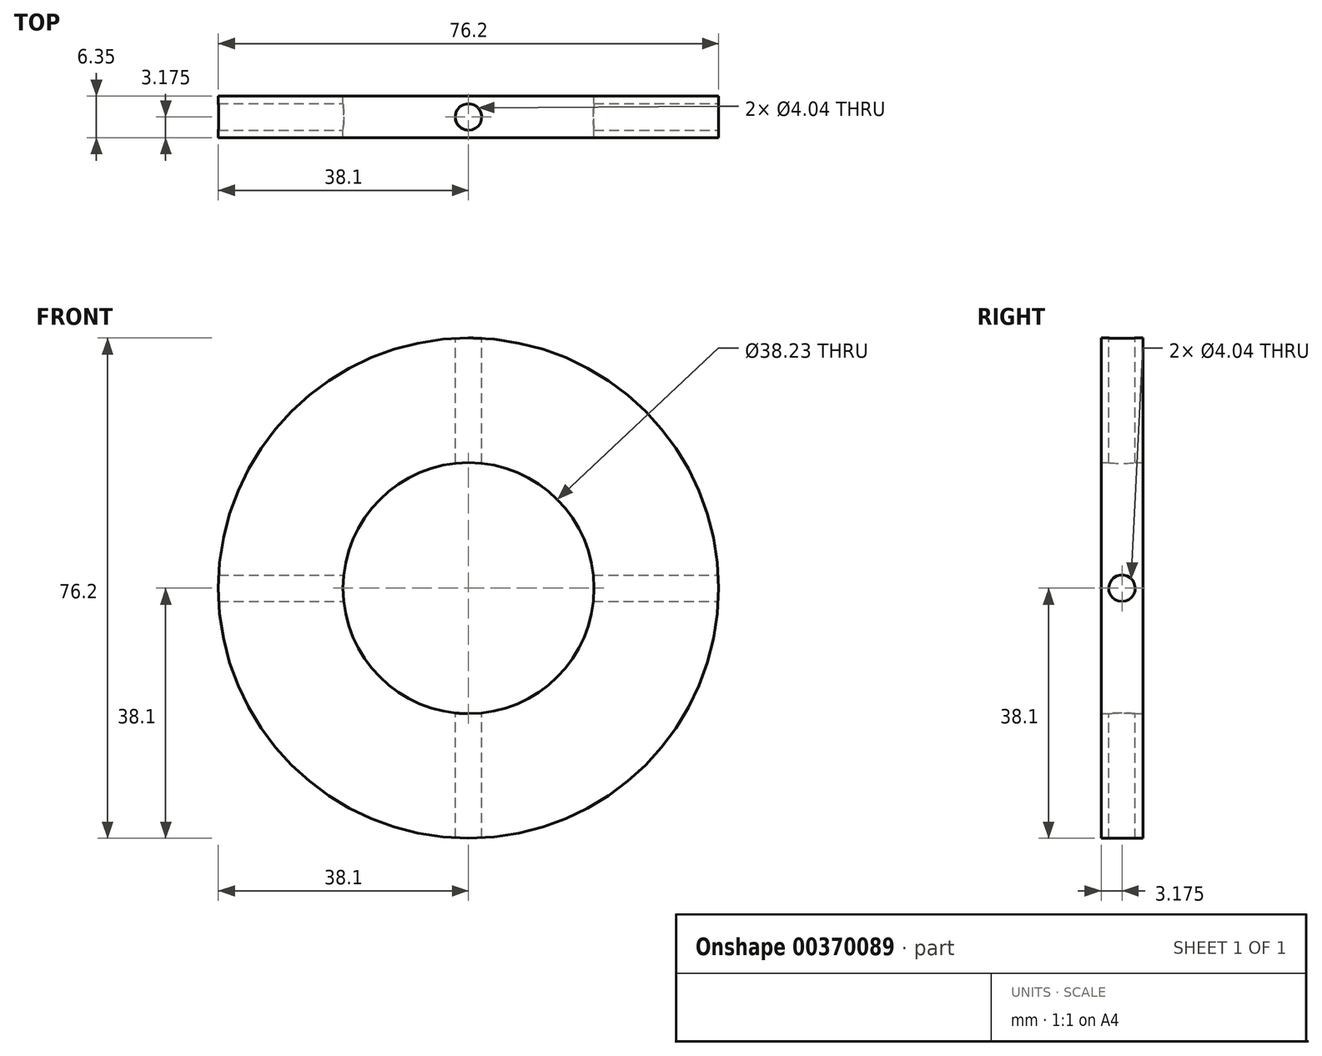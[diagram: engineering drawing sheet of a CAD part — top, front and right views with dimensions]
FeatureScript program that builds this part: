
annotation { "Feature Type Name" : "Feature", "Feature Type Description" : "" }
export const myFeature = defineFeature(function(context is Context, id is Id, definition is map)
    precondition{}
    {
        {
            var Q0;
            Q0=qCreatedBy(makeId("Front.planeOp"),FACE);
            var sketch = newSketch(context, id + "F0", { "sketchPlane" : qUnion([Q0])});
            skCircle(sketch, "E0", {"center": v(0, 0) * mm, "radius": 19.11 * mm});
            skCircle(sketch, "E1", {"center": v(0, 0) * mm, "radius": 38.1 * mm});
            skSolve(sketch);
        }
        {
            var Q0;
            Q0=makeQuery(id+"F0.imprint","IMPRINT",FACE,{"disambiguationData":[TD([[makeQuery(id+"F0.imprint","IMPRINT",EDGE,{"derivedFrom":sQuery(id+"F0.wireOp",EDGE,"E0")}),-1.0]])]});
            extrude(context, id + "F1", {"entities" : qUnion([Q0]), "depth" : 6.35 * mm});
        }
        {
            var Q0;
            Q0=qCreatedBy(makeId("Top.planeOp"),FACE);
            cPlane(context, id + "F2", {"entities" : qUnion([Q0]), "cplaneType" : CPlaneType.OFFSET, "offset" : 38.1 * mm, "width" : 152.4 * mm, "height" : 152.4 * mm});
        }
        {
            var Q0;
            Q0=qCreatedBy(id+"F2.planeOp",FACE);
            var sketch = newSketch(context, id + "F3", { "sketchPlane" : qUnion([Q0])});
            skLineSegment(sketch, "E2", {"start": v(0, 0) * mm, "end": v(0, -3.18) * mm});
            skSolve(sketch);
        }
        {
            var Q0;
            Q0=sQuery(id+"F3.wireOp",VERTEX,"E2.end");
            var Q1;
            Q1=makeQuery(id+"F1.opExtrude","SWEPT_BODY",BODY,{"disambiguationData":[OSD([sQuery(id+"F0.wireOp",EDGE,"E0"),sQuery(id+"F0.wireOp",EDGE,"E1")])]});
            hole(context, id + "F4", {"style" : HoleStyle.SIMPLE, "endStyle" : HoleEndStyle.THROUGH, "standardTappedOrClearance" : lookupTablePath({ "standard" : "ANSI", "engagement" : "75%", "pitch" : "32 tpi", "size" : "#10", "type" : "Tapped" }), "standardBlindInLast" : lookupTablePath({ "standard" : "ANSI", "engagement" : "75%", "pitch" : "32 tpi", "size" : "#10", "type" : "Tapped" }), "holeDiameter" : 4.04 * mm, "showTappedDepth" : true, "isTappedThrough" : true, "tappedDepth" : 12.7 * mm, "tapClearance" : 3, "locations" : qUnion([Q0]), "scope" : qUnion([Q1]), "majorDiameter" : 4.83 * mm});
        }
        {
            var Q0;
            Q0=qCreatedBy(makeId("Right.planeOp"),FACE);
            cPlane(context, id + "F5", {"entities" : qUnion([Q0]), "cplaneType" : CPlaneType.OFFSET, "offset" : 38.1 * mm, "width" : 152.4 * mm, "height" : 152.4 * mm});
        }
        {
            var Q0;
            Q0=qCreatedBy(id+"F5.planeOp",FACE);
            var sketch = newSketch(context, id + "F6", { "sketchPlane" : qUnion([Q0])});
            skLineSegment(sketch, "E3", {"start": v(0, 0) * mm, "end": v(-3.18, 0) * mm});
            skSolve(sketch);
        }
        {
            var Q0;
            Q0=sQuery(id+"F6.wireOp",VERTEX,"E3.end");
            var Q1;
            Q1=makeQuery(id+"F1.opExtrude","SWEPT_BODY",BODY,{"disambiguationData":[OSD([sQuery(id+"F0.wireOp",EDGE,"E0"),sQuery(id+"F0.wireOp",EDGE,"E1")])]});
            hole(context, id + "F7", {"style" : HoleStyle.SIMPLE, "endStyle" : HoleEndStyle.THROUGH, "standardTappedOrClearance" : lookupTablePath({ "standard" : "ANSI", "engagement" : "75%", "pitch" : "32 tpi", "size" : "#10", "type" : "Tapped" }), "standardBlindInLast" : lookupTablePath({ "standard" : "ANSI", "engagement" : "75%", "pitch" : "32 tpi", "size" : "#10", "type" : "Tapped" }), "holeDiameter" : 4.04 * mm, "showTappedDepth" : true, "isTappedThrough" : true, "tappedDepth" : 12.7 * mm, "tapClearance" : 3, "locations" : qUnion([Q0]), "scope" : qUnion([Q1]), "majorDiameter" : 4.83 * mm});
        }
    });
